# Revit family: 0048791
name_source: partatom
category: Lighting Fixtures
revit_build: Autodesk Revit 2017 (Build: 20190507_1515(x64)
units: mm (PartAtom-declared; Revit-internal decimal feet)

## family parameters
Cut with Voids When Loaded = No
Host = Face
Light Source = Yes
OmniClass Number = 23.80.70.11.14
OmniClass Title = General Luminaries, Directional
Part Type = Normal
Room Calculation Point = No
Round Connector Dimension = Use Diameter
Shared = No

## types (2) — shared parameters
AccessoryMaterial = Diffuser-Sylvania-Glow
Assembly Code = D5020200
AssetType = Fixed
BodyMaterial = Body-Sylvania-Gray
ClassificationName = Uniclass2015
ClassificationValue = EF_70_80
Color Filter = 16777215
Default Elevation = 1219 mm
Description = Hydroproof, integrated LED chemical resistant weatherproof luminaire, with UV stabilized flat diffuser and linear prisms designed to achieve uniform lit appearance, optimise light output and to reduce glare, stainless steel diffuser clips and fixing brackets for surface and wall mounting. L 1278 mm x W 110 mm x H 78 mm size, GRP housing, PMMA diffuser, DALI dimmable, 3 hour emergency, 4000K, CRI80,  5550 lm, 38 W, 145 lm/W, nominal average life (h):50000, energy class: A++ A+ A Class I,IK02, IP65.
DiffuserMaterial = Diffuser-Sylvania-Transparent
Dimming Lamp Color Temperature Shift = <None>
DimmingControlOptions = Dimmable
DocumentationLiterature = http://www.sylvania-lighting.com
DurationUnit = hours
ElectricShockClassification = Class I
Emit Shape Visible in Rendering = No
Emit from Rectangle Length = 1252 mm  [stored 4.10761 ft]
Emit from Rectangle Width = 90 mm  [stored 0.295276 ft]
ExpectedLife = 50000
IfcExportAs = IfcLightFixtureType
IfcExportType = IfcLightFixtureType
ImpactProtectionIndex = IK02
IngressProtection = IP65
InputNominalFrequency = DC/50/60 Hz
InputVoltage = 220-240V~
Keynote = 16500
Lamp = LED
LampColourRenderingIndex = 80
LampColourTemperature = 4000 K
LampMacAdamStep = 3
LampsType = LED
Length = 1272 mm  [stored 4.17323 ft]
Manufacturer = Feilo Sylvania
ManufacturerName = Feilo Sylvania
Material = grp housing, pmma diffuser
Model = HYDROPROOF LED G3 1200mm T 4K DALI E3 SSH01
ModelNumber = 0048791
ModelReference = HYDROPROOF LED G3 1200mm T 4K DALI E3 SSH01
Name = HYDROPROOF LED G3 1200mm T 4K DALI E3 SSH01
NominalHeight = 78 mm  [stored 0.255906 ft]
NominalLength = 1278 mm  [stored 4.19291 ft]
ReflectorMaterial = <By Category>
Tilt Angle = -90.00°
Type Image = <None>
TypeName = HYDROPROOF LED G3 1200mm T 4K DALI E3 SSH01
URL = http://www.sylvania-lighting.com
Voltage = 230 V
Weight = 2.36 kg
Width = 110 mm  [stored 0.360892 ft]
zero-valued in all types: Cost, NominalWidth, PowerFactor

## per-type parameters (varying)
| type | Apparent Load | LampNominalLuminous | LuminousEfficacy | Photometric Web File | PowerConsumption |
| 0048791 HYDROPROOF LED G3 1200mm T 4K DALI E3 SSH01 Emergency mode | 2 VA | 270 lm | 145 lm/W | 0048791EM.ies | 1.862 W |
| 0048791 HYDROPROOF LED G3 1200mm T 4K DALI E3 SSH01 | 40 VA | 5550 lm | 137.7 lm/W | 0048791.ies | 40 W |

note: [stored X ft] marks values corroborated as IEEE doubles in the binary element streams (Revit-internal decimal feet)

## geometry (parser evidence)
native form markers: Sweep x5
no freeform markers — native parametric forms only
